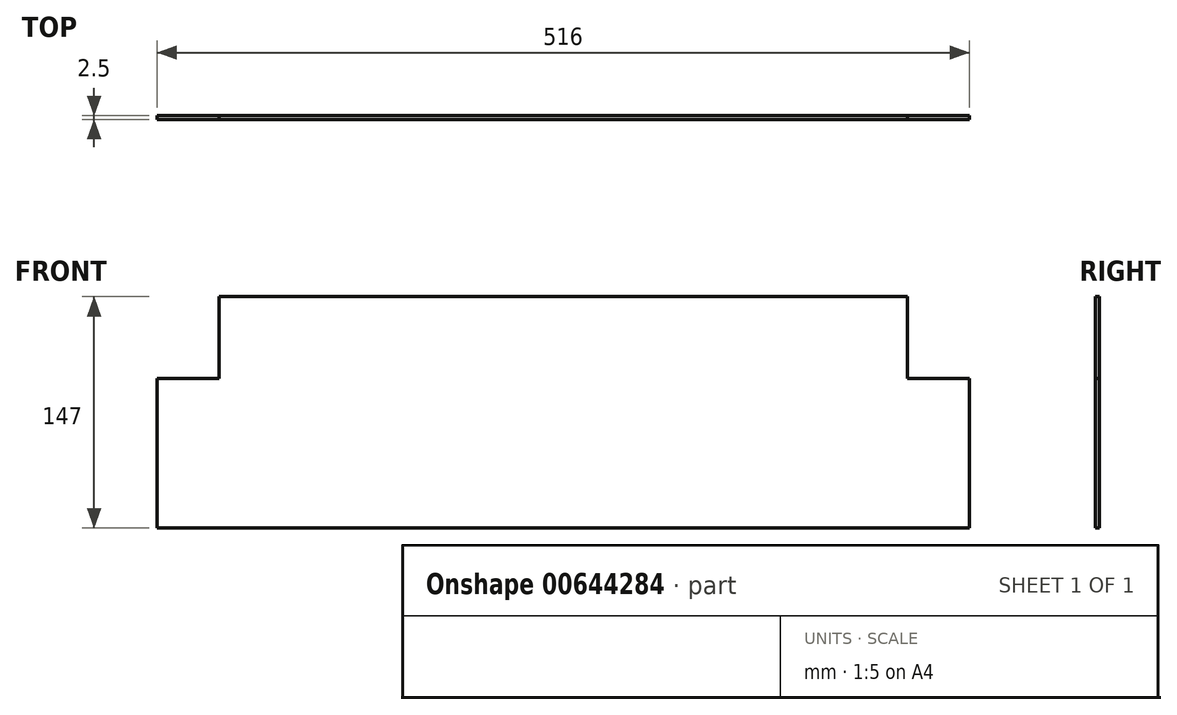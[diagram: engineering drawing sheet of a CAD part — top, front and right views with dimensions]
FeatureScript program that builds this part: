
annotation { "Feature Type Name" : "Feature", "Feature Type Description" : "" }
export const myFeature = defineFeature(function(context is Context, id is Id, definition is map)
    precondition{}
    {
        {
            var Q0;
            Q0=qCreatedBy(makeId("Front.planeOp"),FACE);
            var sketch = newSketch(context, id + "F0", { "sketchPlane" : qUnion([Q0])});
            skLineSegment(sketch, "E0", {"start": v(-218.5, 95) * mm, "end": v(-218.5, 147) * mm});
            skLineSegment(sketch, "E1", {"start": v(-218.5, 147) * mm, "end": v(218.5, 147) * mm});
            skLineSegment(sketch, "E2", {"start": v(218.5, 147) * mm, "end": v(218.5, 95) * mm});
            skLineSegment(sketch, "E3", {"start": v(218.5, 95) * mm, "end": v(258, 95) * mm});
            skLineSegment(sketch, "E4", {"start": v(258, 95) * mm, "end": v(258, 0) * mm});
            skLineSegment(sketch, "E5", {"start": v(-258, 0) * mm, "end": v(-258, 95) * mm});
            skLineSegment(sketch, "E6", {"start": v(-258, 95) * mm, "end": v(-218.5, 95) * mm});
            skLineSegment(sketch, "E7", {"start": v(-218.5, 137) * mm, "end": v(218.5, 137) * mm, "construction": true});
            skLineSegment(sketch, "E8", {"start": v(-258, 0) * mm, "end": v(258, 0) * mm});
            skLineSegment(sketch, "E9", {"start": v(-218.5, 95) * mm, "end": v(-218.5, 0) * mm, "construction": true});
            skLineSegment(sketch, "E10", {"start": v(-218.5, 97.5) * mm, "end": v(-258, 97.5) * mm, "construction": true});
            skLineSegment(sketch, "E11.bottom", {"start": v(-218.5, 95) * mm, "end": v(-217.5, 95) * mm, "construction": true});
            skLineSegment(sketch, "E11.top", {"start": v(-218.5, 0) * mm, "end": v(-217.5, 0) * mm, "construction": true});
            skLineSegment(sketch, "E11.right", {"start": v(-217.5, 95) * mm, "end": v(-217.5, 0) * mm, "construction": true});
            skLineSegment(sketch, "E12.bottom", {"start": v(-218.5, 97.5) * mm, "end": v(218.5, 97.5) * mm, "construction": true});
            skLineSegment(sketch, "E12.top", {"start": v(-218.5, 96.5) * mm, "end": v(218.5, 96.5) * mm, "construction": true});
            skLineSegment(sketch, "E12.left", {"start": v(-218.5, 97.5) * mm, "end": v(-218.5, 96.5) * mm, "construction": true});
            skLineSegment(sketch, "E12.right", {"start": v(218.5, 97.5) * mm, "end": v(218.5, 96.5) * mm, "construction": true});
            skLineSegment(sketch, "E13", {"start": v(-216, 137) * mm, "end": v(-216, 97.5) * mm, "construction": true});
            skLineSegment(sketch, "E14.bottom", {"start": v(-258, 0) * mm, "end": v(-218.5, 0) * mm, "construction": true});
            skLineSegment(sketch, "E14.top", {"start": v(-258, -2.5) * mm, "end": v(-218.5, -2.5) * mm, "construction": true});
            skLineSegment(sketch, "E14.left", {"start": v(-258, 0) * mm, "end": v(-258, -2.5) * mm, "construction": true});
            skLineSegment(sketch, "E14.right", {"start": v(-218.5, 0) * mm, "end": v(-218.5, -2.5) * mm, "construction": true});
            skSolve(sketch);
        }
        {
            var Q0;
            Q0=makeQuery(id+"F0.imprint","IMPRINT",FACE,{"disambiguationData":[TD([[makeQuery(id+"F0.imprint","IMPRINT",EDGE,{"derivedFrom":sQuery(id+"F0.wireOp",EDGE,"E0")}),-1.0]])]});
            extrude(context, id + "F1", {"entities" : qUnion([Q0]), "depth" : 2.5 * mm, "offsetDistance" : 25 * mm});
        }
    });
